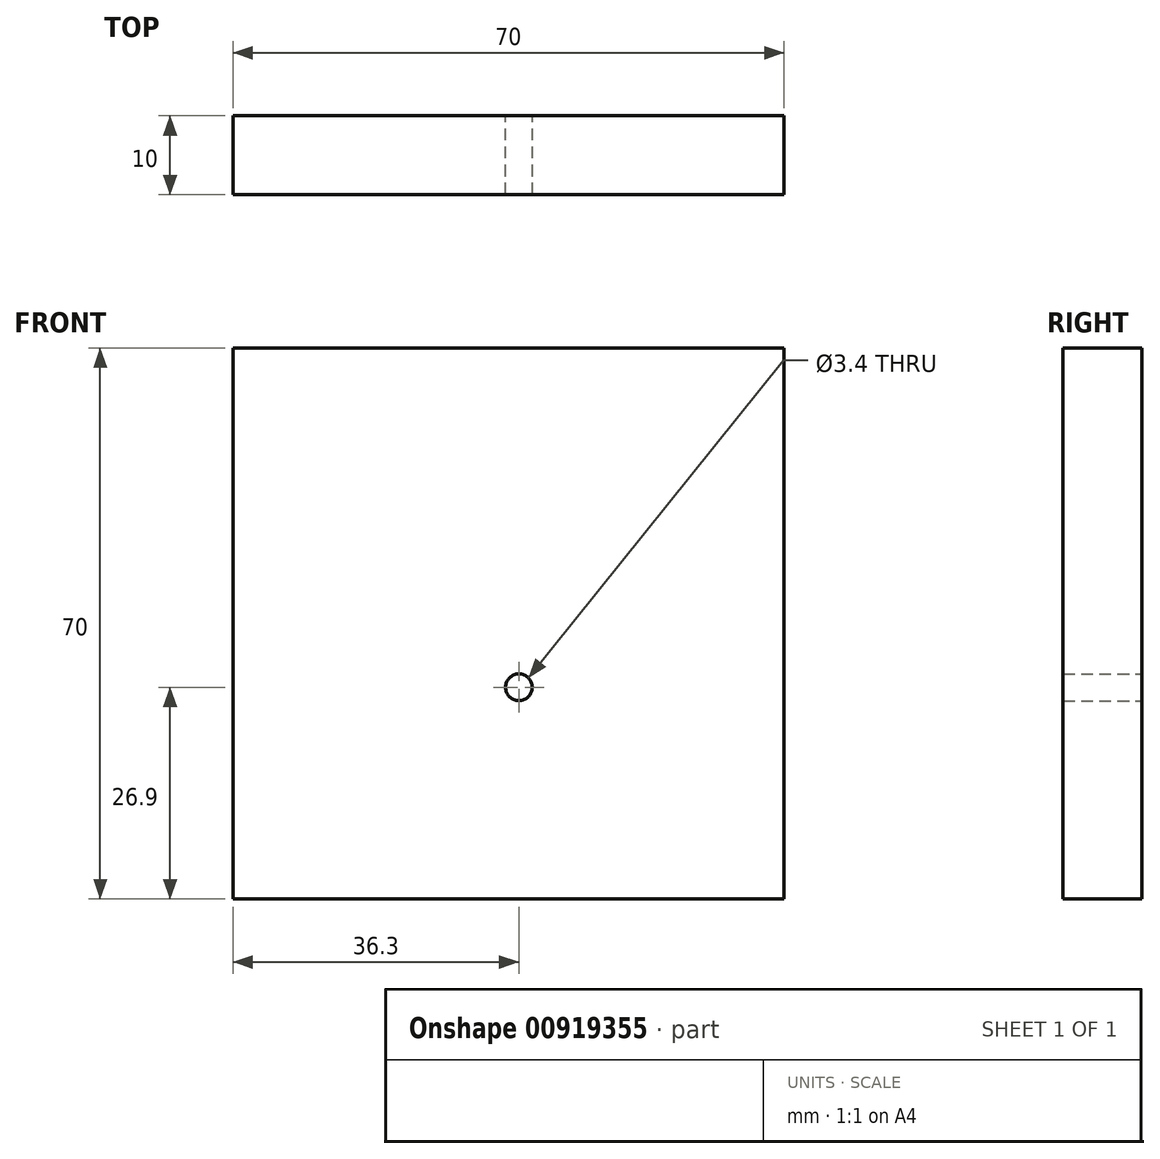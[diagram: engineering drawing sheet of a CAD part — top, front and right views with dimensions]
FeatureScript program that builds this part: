
annotation { "Feature Type Name" : "Feature", "Feature Type Description" : "" }
export const myFeature = defineFeature(function(context is Context, id is Id, definition is map)
    precondition{}
    {
        {
            var Q0;
            Q0=qCreatedBy(makeId("Front.planeOp"),FACE);
            var sketch = newSketch(context, id + "F0", { "sketchPlane" : qUnion([Q0])});
            skLineSegment(sketch, "E0.bottom", {"start": v(35, -35) * mm, "end": v(-35, -35) * mm});
            skLineSegment(sketch, "E0.top", {"start": v(35, 35) * mm, "end": v(-35, 35) * mm});
            skLineSegment(sketch, "E0.left", {"start": v(35, -35) * mm, "end": v(35, 35) * mm});
            skLineSegment(sketch, "E0.right", {"start": v(-35, -35) * mm, "end": v(-35, 35) * mm});
            skPoint(sketch, "E1", {"position": v(0, 0) * mm});
            skPoint(sketch, "E2", {"position": v(1.3, -8.1) * mm});
            skSolve(sketch);
        }
        {
            var Q0;
            Q0 = qSketchRegion(id + "F0", true);
            extrude(context, id + "F1", {"entities" : qUnion([Q0]), "depth" : 10 * mm, "offsetDistance" : 25 * mm});
        }
        {
            var Q0;
            Q0=sQuery(id+"F0.wireOp",VERTEX,"E2");
            var Q1;
            Q1=makeQuery(id+"F1.opExtrude","SWEPT_BODY",BODY,{"disambiguationData":[OSD([sQuery(id+"F0.wireOp",EDGE,"E0.bottom"),sQuery(id+"F0.wireOp",EDGE,"E0.top"),sQuery(id+"F0.wireOp",EDGE,"E0.left"),sQuery(id+"F0.wireOp",EDGE,"E0.right")])]});
            hole(context, id + "F2", {"style" : HoleStyle.SIMPLE, "endStyle" : HoleEndStyle.THROUGH, "oppositeDirection" : true, "holeDiameter" : 3.4 * mm, "majorDiameter" : 5 * mm, "isTappedThrough" : true, "tappedDepth" : 12 * mm, "tapClearance" : 3, "locations" : qUnion([Q0]), "scope" : qUnion([Q1])});
        }
    });
